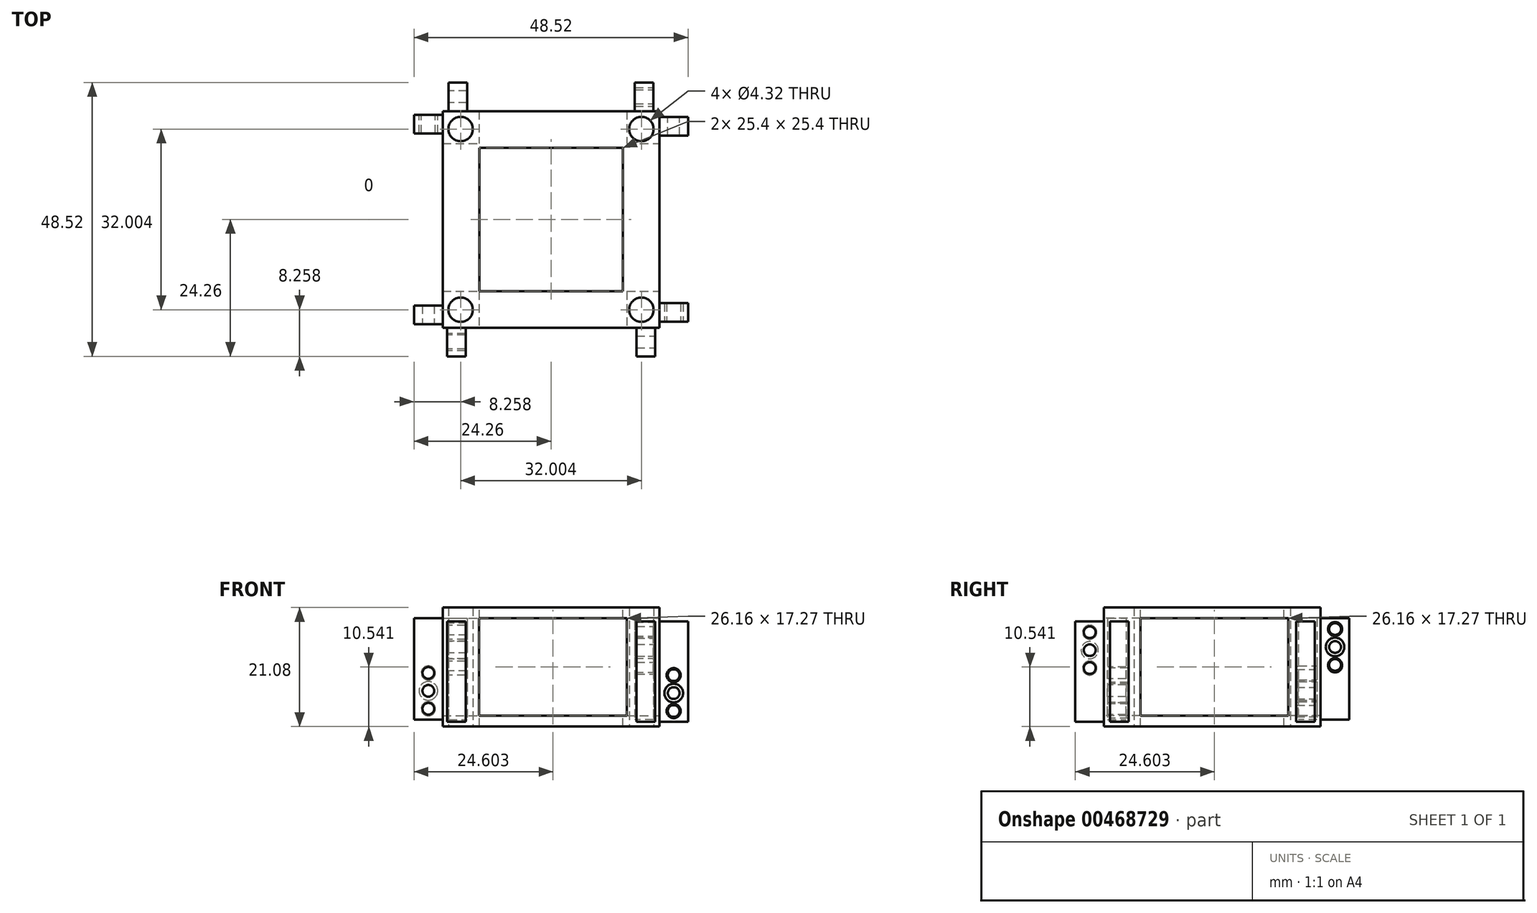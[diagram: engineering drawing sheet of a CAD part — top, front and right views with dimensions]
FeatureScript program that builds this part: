
annotation { "Feature Type Name" : "Feature", "Feature Type Description" : "" }
export const myFeature = defineFeature(function(context is Context, id is Id, definition is map)
    precondition{}
    {
        {
            var Q0;
            Q0=qCreatedBy(makeId("Top.planeOp"),FACE);
            var sketch = newSketch(context, id + "F0", { "sketchPlane" : qUnion([Q0])});
            skLineSegment(sketch, "E0.bottom", {"start": v(-17.9, 19.18) * mm, "end": v(17.9, 19.18) * mm});
            skLineSegment(sketch, "E0.top", {"start": v(-17.9, -19.18) * mm, "end": v(17.9, -19.18) * mm});
            skLineSegment(sketch, "E0.left", {"start": v(-19.18, 17.9) * mm, "end": v(-19.18, -17.9) * mm});
            skLineSegment(sketch, "E0.right", {"start": v(19.18, 17.9) * mm, "end": v(19.18, -17.9) * mm});
            skCircle(sketch, "E1", {"center": v(-16, 16) * mm, "radius": 2.16 * mm});
            skCircle(sketch, "E2", {"center": v(-16, -16) * mm, "radius": 2.16 * mm});
            skCircle(sketch, "E3", {"center": v(16, -16) * mm, "radius": 2.16 * mm});
            skCircle(sketch, "E4", {"center": v(16, 16) * mm, "radius": 2.16 * mm});
            skPoint(sketch, "E5.visualSharp", {"position": v(-19.18, 19.18) * mm});
            skPoint(sketch, "E6.visualSharp", {"position": v(19.18, 19.18) * mm});
            skPoint(sketch, "E7.visualSharp", {"position": v(19.18, -19.18) * mm});
            skLineSegment(sketch, "E8", {"start": v(-16, 16) * mm, "end": v(-16, -16) * mm, "construction": true});
            skPoint(sketch, "E9.middle", {"position": v(-16, 0) * mm});
            skLineSegment(sketch, "E10", {"start": v(-16, -16) * mm, "end": v(16, -16) * mm, "construction": true});
            skLineSegment(sketch, "E11", {"start": v(-19.18, -17.9) * mm, "end": v(-19.18, -19.18) * mm});
            skLineSegment(sketch, "E12", {"start": v(-17.9, -19.18) * mm, "end": v(-19.18, -19.18) * mm});
            skLineSegment(sketch, "E13", {"start": v(19.18, -17.9) * mm, "end": v(19.18, -19.18) * mm});
            skLineSegment(sketch, "E14", {"start": v(17.9, -19.18) * mm, "end": v(19.18, -19.18) * mm});
            skLineSegment(sketch, "E15", {"start": v(17.9, 19.18) * mm, "end": v(19.18, 19.18) * mm});
            skLineSegment(sketch, "E16", {"start": v(19.18, 17.9) * mm, "end": v(19.18, 19.18) * mm});
            skLineSegment(sketch, "E17", {"start": v(-19.18, 17.9) * mm, "end": v(-19.18, 19.18) * mm});
            skLineSegment(sketch, "E18", {"start": v(-19.18, 19.18) * mm, "end": v(-17.9, 19.18) * mm});
            skSolve(sketch);
        }
        {
            var Q0;
            Q0=makeQuery(id+"F0.imprint","IMPRINT",FACE,{"disambiguationData":[TD([[makeQuery(id+"F0.imprint","IMPRINT",EDGE,{"derivedFrom":sQuery(id+"F0.wireOp",EDGE,"E0.bottom")}),-1.0]])]});
            extrude(context, id + "F1", {"entities" : qUnion([Q0]), "depth" : 21.08 * mm});
        }
        {
            var Q0;
            Q0=makeQuery(id+"F1.opExtrude","SWEPT_FACE",FACE,{"disambiguationData":[OSD([sQuery(id+"F0.wireOp",EDGE,"E0.top")])]});
            var sketch = newSketch(context, id + "F2", { "sketchPlane" : qUnion([Q0])});
            skLineSegment(sketch, "E19.bottom", {"start": v(-12.74, 19.18) * mm, "end": v(13.42, 19.18) * mm});
            skLineSegment(sketch, "E19.top", {"start": v(-12.74, 1.9) * mm, "end": v(13.42, 1.9) * mm});
            skLineSegment(sketch, "E19.left", {"start": v(-12.74, 19.18) * mm, "end": v(-12.74, 1.9) * mm});
            skLineSegment(sketch, "E19.right", {"start": v(13.42, 19.18) * mm, "end": v(13.42, 1.9) * mm});
            skLineSegment(sketch, "E20.bottom", {"start": v(-18.42, 18.62) * mm, "end": v(-17.78, 18.62) * mm});
            skLineSegment(sketch, "E20.top", {"start": v(-18.42, 0.85) * mm, "end": v(-17.78, 0.85) * mm});
            skLineSegment(sketch, "E20.left", {"start": v(-17.78, 18.62) * mm, "end": v(-17.78, 0.85) * mm});
            skLineSegment(sketch, "E20.right", {"start": v(-18.41, 18.62) * mm, "end": v(-18.41, 0.85) * mm});
            skLineSegment(sketch, "E21.MirrorCS", {"start": v(18.41, 18.62) * mm, "end": v(17.78, 18.62) * mm});
            skLineSegment(sketch, "E22.MirrorCS", {"start": v(17.78, 18.62) * mm, "end": v(17.78, 0.85) * mm});
            skLineSegment(sketch, "E23.MirrorCS", {"start": v(18.41, 18.62) * mm, "end": v(18.41, 0.85) * mm});
            skLineSegment(sketch, "E24.MirrorCS", {"start": v(18.41, 0.85) * mm, "end": v(17.78, 0.85) * mm});
            skSolve(sketch);
        }
        {
            var Q0;
            Q0=makeQuery(id+"F1.opExtrude","SWEPT_FACE",FACE,{"disambiguationData":[OSD([sQuery(id+"F0.wireOp",EDGE,"E0.right")])]});
            var sketch = newSketch(context, id + "F3", { "sketchPlane" : qUnion([Q0])});
            skLineSegment(sketch, "E25.bottom", {"start": v(-12.74, 19.18) * mm, "end": v(13.42, 19.18) * mm});
            skLineSegment(sketch, "E25.top", {"start": v(-12.74, 1.9) * mm, "end": v(13.42, 1.9) * mm});
            skLineSegment(sketch, "E25.left", {"start": v(-12.74, 19.18) * mm, "end": v(-12.74, 1.9) * mm});
            skLineSegment(sketch, "E25.right", {"start": v(13.42, 19.18) * mm, "end": v(13.42, 1.9) * mm});
            skLineSegment(sketch, "E26.bottom", {"start": v(-18.15, 18.63) * mm, "end": v(-17.51, 18.63) * mm});
            skLineSegment(sketch, "E26.top", {"start": v(-18.15, 0.85) * mm, "end": v(-17.51, 0.85) * mm});
            skLineSegment(sketch, "E26.left", {"start": v(-17.51, 18.63) * mm, "end": v(-17.51, 0.85) * mm});
            skLineSegment(sketch, "E26.right", {"start": v(-18.15, 18.63) * mm, "end": v(-18.15, 0.85) * mm});
            skLineSegment(sketch, "E27.MirrorCS", {"start": v(18.15, 18.63) * mm, "end": v(17.51, 18.63) * mm});
            skLineSegment(sketch, "E28.MirrorCS", {"start": v(18.15, 18.63) * mm, "end": v(18.15, 0.85) * mm});
            skLineSegment(sketch, "E29.MirrorCS", {"start": v(17.51, 18.63) * mm, "end": v(17.51, 0.85) * mm});
            skLineSegment(sketch, "E30.MirrorCS", {"start": v(18.15, 0.85) * mm, "end": v(17.51, 0.85) * mm});
            skSolve(sketch);
        }
        {
            var Q0;
            Q0=makeQuery(id+"F2.imprint","IMPRINT",FACE,{"disambiguationData":[TD([[makeQuery(id+"F2.imprint","IMPRINT",EDGE,{"derivedFrom":sQuery(id+"F2.wireOp",EDGE,"E19.bottom")}),-1.0]])]});
            extrude(context, id + "F4", {"entities" : qUnion([Q0]), "operationType" : NewBodyOperationType.REMOVE, "endBound" : BoundingType.THROUGH_ALL, "oppositeDirection" : true, "depth" : 25.4 * mm});
        }
        {
            var Q0;
            Q0=makeQuery(id+"F3.imprint","IMPRINT",FACE,{"disambiguationData":[TD([[makeQuery(id+"F3.imprint","IMPRINT",EDGE,{"derivedFrom":sQuery(id+"F3.wireOp",EDGE,"E25.bottom")}),-1.0]])]});
            extrude(context, id + "F5", {"entities" : qUnion([Q0]), "operationType" : NewBodyOperationType.REMOVE, "endBound" : BoundingType.THROUGH_ALL, "oppositeDirection" : true, "depth" : 25.4 * mm});
        }
        {
            var Q0;
            Q0=makeQuery(id+"F2.imprint","IMPRINT",FACE,{"disambiguationData":[TD([[makeQuery(id+"F2.imprint","IMPRINT",EDGE,{"derivedFrom":sQuery(id+"F2.wireOp",EDGE,"E21.MirrorCS")}),1.0]])]});
            var Q1;
            Q1=makeQuery(id+"F2.imprint","IMPRINT",FACE,{"disambiguationData":[TD([[makeQuery(id+"F2.imprint","IMPRINT",EDGE,{"derivedFrom":sQuery(id+"F2.wireOp",EDGE,"E20.bottom")}),-1.0]])]});
            extrude(context, id + "F6", {"entities" : qUnion([Q0, Q1]), "operationType" : NewBodyOperationType.ADD, "depth" : 5.08 * mm});
        }
        {
            var Q0;
            Q0=makeQuery(id+"F3.imprint","IMPRINT",FACE,{"disambiguationData":[TD([[makeQuery(id+"F3.imprint","IMPRINT",EDGE,{"derivedFrom":sQuery(id+"F3.wireOp",EDGE,"E26.bottom")}),-1.0]])]});
            var Q1;
            Q1=makeQuery(id+"F3.imprint","IMPRINT",FACE,{"disambiguationData":[TD([[makeQuery(id+"F3.imprint","IMPRINT",EDGE,{"derivedFrom":sQuery(id+"F3.wireOp",EDGE,"E27.MirrorCS")}),1.0]])]});
            extrude(context, id + "F7", {"entities" : qUnion([Q0, Q1]), "operationType" : NewBodyOperationType.ADD, "depth" : 5.08 * mm});
        }
        {
            var Q0;
            Q0=makeQuery(id+"F1.opExtrude","SWEPT_FACE",FACE,{"disambiguationData":[OSD([sQuery(id+"F0.wireOp",EDGE,"E0.left"),sQuery(id+"F0.wireOp",EDGE,"E11"),sQuery(id+"F0.wireOp",EDGE,"E17")])]});
            var sketch = newSketch(context, id + "F8", { "sketchPlane" : qUnion([Q0])});
            skLineSegment(sketch, "E31.bottom", {"start": v(-18.54, 19.18) * mm, "end": v(-17.9, 19.18) * mm});
            skLineSegment(sketch, "E31.top", {"start": v(-18.54, 1.25) * mm, "end": v(-17.9, 1.25) * mm});
            skLineSegment(sketch, "E31.left", {"start": v(-17.9, 19.18) * mm, "end": v(-17.9, 1.25) * mm});
            skLineSegment(sketch, "E31.right", {"start": v(-18.54, 19.18) * mm, "end": v(-18.54, 1.25) * mm});
            skLineSegment(sketch, "E32.MirrorCS", {"start": v(18.54, 19.18) * mm, "end": v(17.9, 19.18) * mm});
            skLineSegment(sketch, "E33.MirrorCS", {"start": v(18.54, 19.18) * mm, "end": v(18.54, 1.25) * mm});
            skLineSegment(sketch, "E34.MirrorCS", {"start": v(17.9, 19.18) * mm, "end": v(17.9, 1.25) * mm});
            skLineSegment(sketch, "E35.MirrorCS", {"start": v(18.54, 1.25) * mm, "end": v(17.9, 1.25) * mm});
            skSolve(sketch);
        }
        {
            var Q0;
            Q0=makeQuery(id+"F1.opExtrude","SWEPT_FACE",FACE,{"disambiguationData":[OSD([sQuery(id+"F0.wireOp",EDGE,"E0.bottom"),sQuery(id+"F0.wireOp",EDGE,"E15"),sQuery(id+"F0.wireOp",EDGE,"E18")])]});
            var sketch = newSketch(context, id + "F9", { "sketchPlane" : qUnion([Q0])});
            skLineSegment(sketch, "E36.bottom", {"start": v(-18.15, 19.18) * mm, "end": v(-14.84, 19.18) * mm});
            skLineSegment(sketch, "E36.top", {"start": v(-18.15, 1.25) * mm, "end": v(-14.84, 1.25) * mm});
            skLineSegment(sketch, "E36.left", {"start": v(-14.84, 19.18) * mm, "end": v(-14.84, 1.25) * mm});
            skLineSegment(sketch, "E36.right", {"start": v(-18.15, 19.18) * mm, "end": v(-18.15, 1.25) * mm});
            skLineSegment(sketch, "E37.MirrorCS", {"start": v(18.15, 19.18) * mm, "end": v(14.84, 19.18) * mm});
            skLineSegment(sketch, "E38.MirrorCS", {"start": v(18.15, 19.18) * mm, "end": v(18.15, 1.25) * mm});
            skLineSegment(sketch, "E39.MirrorCS", {"start": v(14.84, 19.18) * mm, "end": v(14.84, 1.25) * mm});
            skLineSegment(sketch, "E40.MirrorCS", {"start": v(18.15, 1.25) * mm, "end": v(14.84, 1.25) * mm});
            skSolve(sketch);
        }
        {
            var Q0;
            Q0=makeQuery(id+"F9.imprint","IMPRINT",FACE,{"disambiguationData":[TD([[makeQuery(id+"F9.imprint","IMPRINT",EDGE,{"derivedFrom":sQuery(id+"F9.wireOp",EDGE,"E36.bottom")}),-1.0]])]});
            var Q1;
            Q1=makeQuery(id+"F9.imprint","IMPRINT",FACE,{"disambiguationData":[TD([[makeQuery(id+"F9.imprint","IMPRINT",EDGE,{"derivedFrom":sQuery(id+"F9.wireOp",EDGE,"E37.MirrorCS")}),1.0]])]});
            extrude(context, id + "F10", {"entities" : qUnion([Q0, Q1]), "operationType" : NewBodyOperationType.ADD, "depth" : 5.08 * mm});
        }
        {
            var Q0;
            Q0=makeQuery(id+"F8.imprint","IMPRINT",FACE,{"disambiguationData":[TD([[makeQuery(id+"F8.imprint","IMPRINT",EDGE,{"derivedFrom":sQuery(id+"F8.wireOp",EDGE,"E31.bottom")}),-1.0]])]});
            var Q1;
            Q1=makeQuery(id+"F8.imprint","IMPRINT",FACE,{"disambiguationData":[TD([[makeQuery(id+"F8.imprint","IMPRINT",EDGE,{"derivedFrom":sQuery(id+"F8.wireOp",EDGE,"E32.MirrorCS")}),1.0]])]});
            extrude(context, id + "F11", {"entities" : qUnion([Q0, Q1]), "operationType" : NewBodyOperationType.ADD, "depth" : 5.08 * mm});
        }
        {
            var Q0;
            Q0=makeQuery(id+"F11.opExtrude","SWEPT_FACE",FACE,{"disambiguationData":[OSD([sQuery(id+"F8.wireOp",EDGE,"E31.right")])]});
            var sketch = newSketch(context, id + "F12", { "sketchPlane" : qUnion([Q0])});
            skCircle(sketch, "E41", {"center": v(21.72, 3.15) * mm, "radius": 1.24 * mm});
            skPoint(sketch, "E41.centerSnap0", {"position": v(21.72, 1.25) * mm});
            skLineSegment(sketch, "E42", {"start": v(21.72, 1.25) * mm, "end": v(21.72, 19.18) * mm, "construction": true});
            skCircle(sketch, "E43", {"center": v(21.72, 6.33) * mm, "radius": 1.65 * mm});
            skCircle(sketch, "E44", {"center": v(21.72, 9.5) * mm, "radius": 1.24 * mm});
            skPoint(sketch, "E45", {"position": v(21.72, 10.21) * mm});
            skSolve(sketch);
        }
        {
            var Q0;
            Q0 = qSketchRegion(id + "F12", true);
            var Q1;
            Q1=sQuery(id+"F12.wireOp",EDGE,"E44");
            var Q2;
            Q2=sQuery(id+"F12.wireOp",EDGE,"E43");
            var Q3;
            Q3=sQuery(id+"F12.wireOp",EDGE,"E41");
            extrude(context, id + "F13", {"entities" : qUnion([Q0]), "operationType" : NewBodyOperationType.REMOVE, "surfaceEntities" : qUnion([Q1, Q2, Q3]), "oppositeDirection" : true, "depth" : 11.43 * mm});
        }
        {
            var Q0;
            Q0=makeQuery(id+"F10.opExtrude","SWEPT_FACE",FACE,{"disambiguationData":[OSD([sQuery(id+"F9.wireOp",EDGE,"E36.right")])]});
            var sketch = newSketch(context, id + "F14", { "sketchPlane" : qUnion([Q0])});
            skLineSegment(sketch, "E46", {"start": v(21.72, 19.18) * mm, "end": v(21.72, 1.25) * mm, "construction": true});
            skCircle(sketch, "E47", {"center": v(21.72, 10.85) * mm, "radius": 1.24 * mm});
            skCircle(sketch, "E48", {"center": v(21.72, 14.1) * mm, "radius": 1.65 * mm});
            skCircle(sketch, "E49", {"center": v(21.72, 17.27) * mm, "radius": 1.24 * mm});
            skSolve(sketch);
        }
        {
            var Q0;
            Q0 = qSketchRegion(id + "F14", true);
            extrude(context, id + "F15", {"entities" : qUnion([Q0]), "operationType" : NewBodyOperationType.REMOVE, "oppositeDirection" : true, "depth" : 11.43 * mm});
        }
        {
            var Q0;
            Q0=makeQuery(id+"F6.opExtrude","SWEPT_FACE",FACE,{"disambiguationData":[OSD([sQuery(id+"F2.wireOp",EDGE,"E20.right")])]});
            var sketch = newSketch(context, id + "F16", { "sketchPlane" : qUnion([Q0])});
            skLineSegment(sketch, "E50", {"start": v(21.72, 18.62) * mm, "end": v(21.72, 0.85) * mm, "construction": true});
            skCircle(sketch, "E51", {"center": v(21.72, 13.54) * mm, "radius": 1.52 * mm});
            skCircle(sketch, "E52", {"center": v(21.72, 10.36) * mm, "radius": 1.24 * mm});
            skCircle(sketch, "E53", {"center": v(21.72, 16.71) * mm, "radius": 1.24 * mm});
            skSolve(sketch);
        }
        {
            var Q0;
            Q0 = qSketchRegion(id + "F16", true);
            extrude(context, id + "F17", {"entities" : qUnion([Q0]), "operationType" : NewBodyOperationType.REMOVE, "oppositeDirection" : true, "depth" : 11.43 * mm});
        }
        {
            var Q0;
            Q0=makeQuery(id+"F6.opExtrude","SWEPT_FACE",FACE,{"disambiguationData":[OSD([sQuery(id+"F2.wireOp",EDGE,"E20.right")])]});
            var sketch = newSketch(context, id + "F18", { "sketchPlane" : qUnion([Q0])});
            skLineSegment(sketch, "E54", {"start": v(21.72, 18.62) * mm, "end": v(21.72, 0.85) * mm, "construction": true});
            skCircle(sketch, "E55", {"center": v(21.72, 3.1) * mm, "radius": 1.02 * mm});
            skCircle(sketch, "E56", {"center": v(21.72, 5.52) * mm, "radius": 1.02 * mm});
            skCircle(sketch, "E57", {"center": v(21.72, 7.58) * mm, "radius": 1.02 * mm});
            skSolve(sketch);
        }
        {
            var Q0;
            Q0=makeQuery(id+"F7.opExtrude","SWEPT_FACE",FACE,{"disambiguationData":[OSD([sQuery(id+"F3.wireOp",EDGE,"E26.right")])]});
            var sketch = newSketch(context, id + "F19", { "sketchPlane" : qUnion([Q0])});
            skLineSegment(sketch, "E58", {"start": v(21.72, 18.63) * mm, "end": v(21.72, 0.85) * mm, "construction": true});
            skCircle(sketch, "E59", {"center": v(21.72, 2.75) * mm, "radius": 1.24 * mm});
            skCircle(sketch, "E60", {"center": v(21.72, 5.93) * mm, "radius": 1.65 * mm});
            skCircle(sketch, "E61", {"center": v(21.72, 9.1) * mm, "radius": 1.24 * mm});
            skSolve(sketch);
        }
        {
            var Q0;
            Q0 = qSketchRegion(id + "F19", true);
            extrude(context, id + "F20", {"entities" : qUnion([Q0]), "operationType" : NewBodyOperationType.REMOVE, "oppositeDirection" : true, "depth" : 11.43 * mm});
        }
        {
            var Q0;
            Q0=makeQuery(id+"F1.opExtrude","CAP_FACE",FACE,{"disambiguationData":[OSD([sQuery(id+"F0.wireOp",EDGE,"E0.bottom"),sQuery(id+"F0.wireOp",EDGE,"E0.top"),sQuery(id+"F0.wireOp",EDGE,"E0.left"),sQuery(id+"F0.wireOp",EDGE,"E0.right"),sQuery(id+"F0.wireOp",EDGE,"E1"),sQuery(id+"F0.wireOp",EDGE,"E2"),sQuery(id+"F0.wireOp",EDGE,"E3"),sQuery(id+"F0.wireOp",EDGE,"E4"),sQuery(id+"F0.wireOp",EDGE,"E11"),sQuery(id+"F0.wireOp",EDGE,"E12"),sQuery(id+"F0.wireOp",EDGE,"E13"),sQuery(id+"F0.wireOp",EDGE,"E14"),sQuery(id+"F0.wireOp",EDGE,"E15"),sQuery(id+"F0.wireOp",EDGE,"E16"),sQuery(id+"F0.wireOp",EDGE,"E17"),sQuery(id+"F0.wireOp",EDGE,"E18")])],"isStart":false});
            var sketch = newSketch(context, id + "F21", { "sketchPlane" : qUnion([Q0])});
            skLineSegment(sketch, "E62.bottom", {"start": v(-16, 16) * mm, "end": v(16, 16) * mm, "construction": true});
            skLineSegment(sketch, "E62.top", {"start": v(-16, -16) * mm, "end": v(16, -16) * mm, "construction": true});
            skLineSegment(sketch, "E62.left", {"start": v(-16, 16) * mm, "end": v(-16, -16) * mm, "construction": true});
            skLineSegment(sketch, "E62.right", {"start": v(16, 16) * mm, "end": v(16, -16) * mm, "construction": true});
            skLineSegment(sketch, "E63.0", {"start": v(-12.7, 12.7) * mm, "end": v(12.7, 12.7) * mm});
            skLineSegment(sketch, "E63.1", {"start": v(-12.7, 12.7) * mm, "end": v(-12.7, -12.7) * mm});
            skLineSegment(sketch, "E63.2", {"start": v(-12.7, -12.7) * mm, "end": v(12.7, -12.7) * mm});
            skLineSegment(sketch, "E63.3", {"start": v(12.7, 12.7) * mm, "end": v(12.7, -12.7) * mm});
            skSolve(sketch);
        }
        {
            var Q0;
            Q0=makeQuery(id+"F21.imprint","IMPRINT",FACE,{"disambiguationData":[TD([[makeQuery(id+"F21.imprint","IMPRINT",EDGE,{"derivedFrom":sQuery(id+"F21.wireOp",EDGE,"E63.0")}),-1.0]])]});
            extrude(context, id + "F22", {"entities" : qUnion([Q0]), "operationType" : NewBodyOperationType.REMOVE, "endBound" : BoundingType.THROUGH_ALL, "oppositeDirection" : true, "depth" : 25.4 * mm});
        }
        {
            var Q0;
            Q0=makeQuery(id+"F11.opExtrude","SWEPT_FACE",FACE,{"disambiguationData":[OSD([sQuery(id+"F8.wireOp",EDGE,"E31.left")])]});
            extrude(context, id + "F23", {"entities" : qUnion([Q0]), "operationType" : NewBodyOperationType.ADD, "depth" : 2.67 * mm});
        }
        {
            var Q0;
            Q0=makeQuery(id+"F11.opExtrude","SWEPT_FACE",FACE,{"disambiguationData":[OSD([sQuery(id+"F8.wireOp",EDGE,"E34.MirrorCS")])]});
            extrude(context, id + "F24", {"entities" : qUnion([Q0]), "operationType" : NewBodyOperationType.ADD, "depth" : 2.67 * mm});
        }
        {
            var Q0;
            Q0=makeQuery(id+"F6.opExtrude","SWEPT_FACE",FACE,{"disambiguationData":[OSD([sQuery(id+"F2.wireOp",EDGE,"E22.MirrorCS")])]});
            extrude(context, id + "F25", {"entities" : qUnion([Q0]), "operationType" : NewBodyOperationType.ADD, "depth" : 2.67 * mm});
        }
        {
            var Q0;
            Q0=makeQuery(id+"F6.opExtrude","SWEPT_FACE",FACE,{"disambiguationData":[OSD([sQuery(id+"F2.wireOp",EDGE,"E20.left")])]});
            extrude(context, id + "F26", {"entities" : qUnion([Q0]), "operationType" : NewBodyOperationType.ADD, "depth" : 2.67 * mm});
        }
        {
            var Q0;
            Q0=makeQuery(id+"F7.opExtrude","SWEPT_FACE",FACE,{"disambiguationData":[OSD([sQuery(id+"F3.wireOp",EDGE,"E26.left")])]});
            extrude(context, id + "F27", {"entities" : qUnion([Q0]), "operationType" : NewBodyOperationType.ADD, "depth" : 2.67 * mm});
        }
        {
            var Q0;
            Q0=makeQuery(id+"F7.opExtrude","SWEPT_FACE",FACE,{"disambiguationData":[OSD([sQuery(id+"F3.wireOp",EDGE,"E29.MirrorCS")])]});
            extrude(context, id + "F28", {"entities" : qUnion([Q0]), "operationType" : NewBodyOperationType.ADD, "depth" : 2.67 * mm});
        }
        {
            var Q0;
            Q0=makeQuery(id+"F7.opExtrude","SWEPT_FACE",FACE,{"disambiguationData":[OSD([sQuery(id+"F3.wireOp",EDGE,"E28.MirrorCS")])]});
            var sketch = newSketch(context, id + "F29", { "sketchPlane" : qUnion([Q0])});
            skCircle(sketch, "E64", {"center": v(-21.72, 5.93) * mm, "radius": 1.04 * mm});
            skCircle(sketch, "E65", {"center": v(-21.72, 9.1) * mm, "radius": 1.04 * mm});
            skCircle(sketch, "E66", {"center": v(-21.72, 2.76) * mm, "radius": 1.04 * mm});
            skLineSegment(sketch, "E67", {"start": v(-21.72, 18.63) * mm, "end": v(-21.72, 0.85) * mm, "construction": true});
            skSolve(sketch);
        }
        {
            var Q0;
            Q0 = qSketchRegion(id + "F29", true);
            extrude(context, id + "F30", {"entities" : qUnion([Q0]), "operationType" : NewBodyOperationType.REMOVE, "oppositeDirection" : true, "depth" : 11.43 * mm});
        }
        {
            var Q0;
            Q0=makeQuery(id+"F10.opExtrude","SWEPT_FACE",FACE,{"disambiguationData":[OSD([sQuery(id+"F9.wireOp",EDGE,"E38.MirrorCS")])]});
            var sketch = newSketch(context, id + "F31", { "sketchPlane" : qUnion([Q0])});
            skSolve(sketch);
        }
        {
            var Q0;
            {var subQ0=sQuery(id+"F9.wireOp",EDGE,"E38.MirrorCS");Q0=makeQuery(id+"F31.imprint","IMPRINT",FACE,{"disambiguationData":[TD([[makeQuery(id+"F31.imprint","IMPRINT",EDGE,{"derivedFrom":makeQuery(id+"F10.opExtrude","CAP_EDGE",EDGE,{"disambiguationData":[OSD([subQ0])],"isStart":false})}),1.0]])]});}
            var sketch = newSketch(context, id + "F32", { "sketchPlane" : qUnion([Q0])});
            skCircle(sketch, "E68", {"center": v(-21.72, 17.27) * mm, "radius": 1.04 * mm});
            skCircle(sketch, "E69", {"center": v(-21.72, 14.1) * mm, "radius": 1.04 * mm});
            skCircle(sketch, "E70", {"center": v(-21.72, 10.92) * mm, "radius": 1.04 * mm});
            skSolve(sketch);
        }
        {
            var Q0;
            Q0 = qSketchRegion(id + "F32", true);
            extrude(context, id + "F33", {"entities" : qUnion([Q0]), "operationType" : NewBodyOperationType.REMOVE, "oppositeDirection" : true, "depth" : 11.43 * mm});
        }
        {
            var Q0;
            Q0=makeQuery(id+"F11.opExtrude","SWEPT_FACE",FACE,{"disambiguationData":[OSD([sQuery(id+"F8.wireOp",EDGE,"E33.MirrorCS")])]});
            var sketch = newSketch(context, id + "F34", { "sketchPlane" : qUnion([Q0])});
            skCircle(sketch, "E71", {"center": v(-21.72, 9.5) * mm, "radius": 1.04 * mm});
            skCircle(sketch, "E72", {"center": v(-21.72, 6.33) * mm, "radius": 1.04 * mm});
            skCircle(sketch, "E73", {"center": v(-21.72, 3.15) * mm, "radius": 1.04 * mm});
            skSolve(sketch);
        }
        {
            var Q0;
            Q0 = qSketchRegion(id + "F34", true);
            extrude(context, id + "F35", {"entities" : qUnion([Q0]), "operationType" : NewBodyOperationType.REMOVE, "oppositeDirection" : true, "depth" : 11.43 * mm});
        }
        {
            var Q0;
            Q0=makeQuery(id+"F6.opExtrude","SWEPT_FACE",FACE,{"disambiguationData":[OSD([sQuery(id+"F2.wireOp",EDGE,"E23.MirrorCS")])]});
            var sketch = newSketch(context, id + "F36", { "sketchPlane" : qUnion([Q0])});
            skCircle(sketch, "E74", {"center": v(-21.72, 16.71) * mm, "radius": 1.04 * mm});
            skCircle(sketch, "E75", {"center": v(-21.72, 13.54) * mm, "radius": 1.04 * mm});
            skCircle(sketch, "E76", {"center": v(-21.72, 10.36) * mm, "radius": 1.04 * mm});
            skSolve(sketch);
        }
        {
            var Q0;
            Q0 = qSketchRegion(id + "F36", true);
            extrude(context, id + "F37", {"entities" : qUnion([Q0]), "operationType" : NewBodyOperationType.REMOVE, "oppositeDirection" : true, "depth" : 11.43 * mm});
        }
    });
